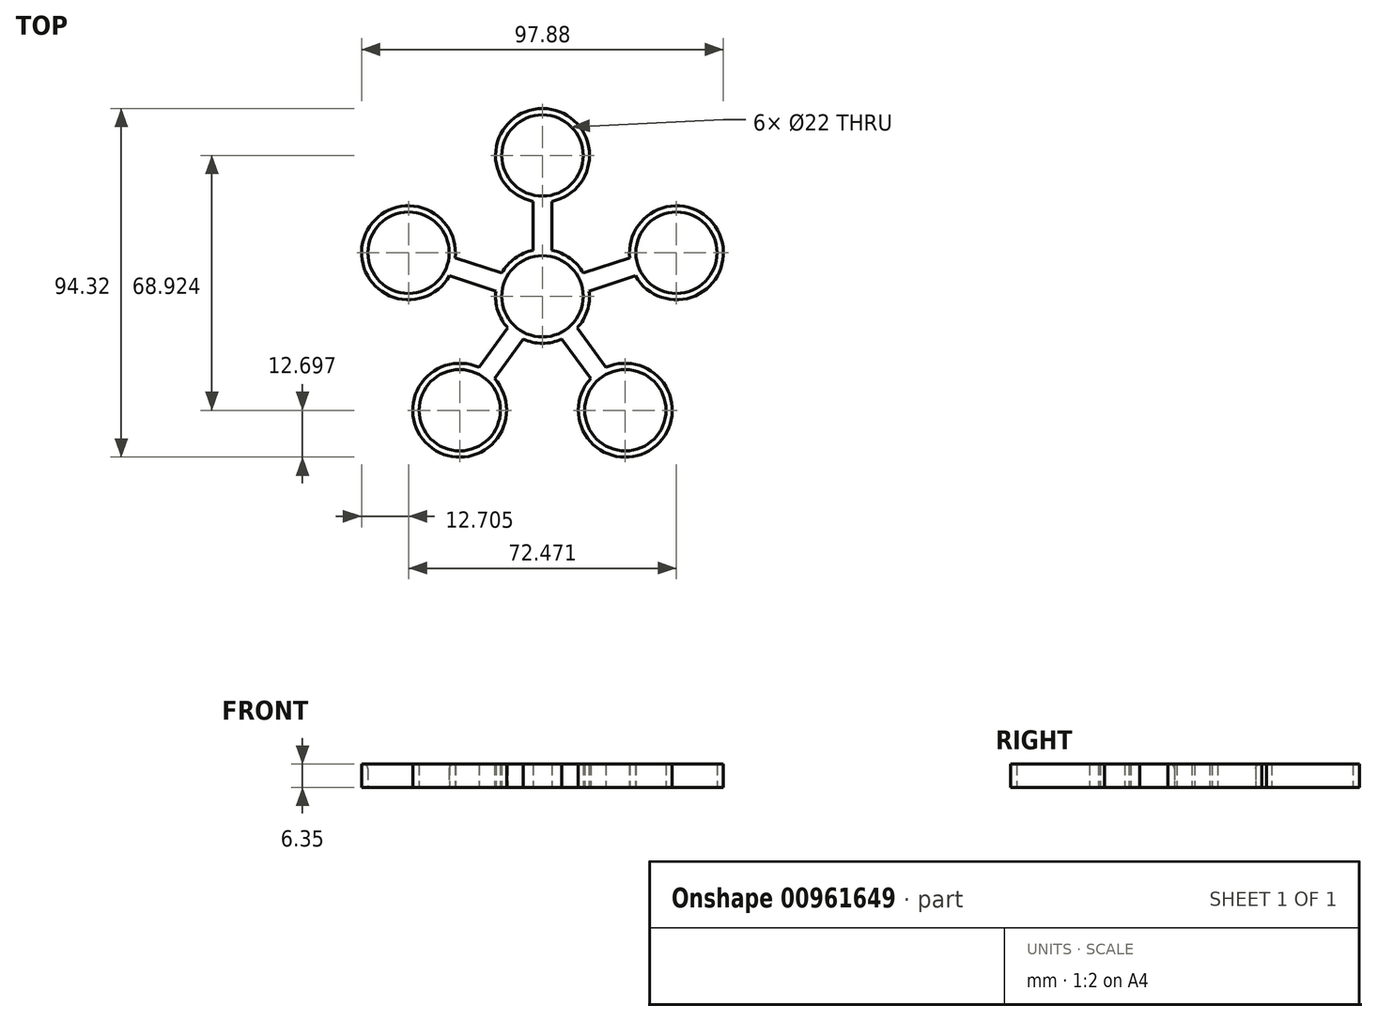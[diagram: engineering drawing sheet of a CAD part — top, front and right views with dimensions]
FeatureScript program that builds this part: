
annotation { "Feature Type Name" : "Feature", "Feature Type Description" : "" }
export const myFeature = defineFeature(function(context is Context, id is Id, definition is map)
    precondition{}
    {
        {
            var Q0;
            Q0=qCreatedBy(makeId("Top.planeOp"),FACE);
            var sketch = newSketch(context, id + "F0", { "sketchPlane" : qUnion([Q0])});
            skCircle(sketch, "E0", {"center": v(0, 0) * mm, "radius": 11 * mm});
            skArc(sketch, "E1", {"start": v(-2.54, 12.44) * mm, "mid": v(-7.46, 10.27) * mm, "end": v(-11.05, 6.26) * mm});
            skArc(sketch, "E2", {"start": v(2.54, 25.66) * mm, "mid": v(0, 50.8) * mm, "end": v(-2.54, 25.66) * mm});
            skCircle(sketch, "E3", {"center": v(0, 38.1) * mm, "radius": 11 * mm});
            skLineSegment(sketch, "E4", {"start": v(2.54, 25.66) * mm, "end": v(2.54, 12.44) * mm});
            skLineSegment(sketch, "E5", {"start": v(-2.54, 25.66) * mm, "end": v(-2.54, 12.44) * mm});
            skLineSegment(sketch, "E6.1.0", {"start": v(-23.62, 10.34) * mm, "end": v(-11.05, 6.26) * mm});
            skLineSegment(sketch, "E6.1.1", {"start": v(-25.19, 5.51) * mm, "end": v(-12.62, 1.43) * mm});
            skArc(sketch, "E6.1.2", {"start": v(-23.62, 10.34) * mm, "mid": v(-48.31, 15.7) * mm, "end": v(-25.19, 5.51) * mm});
            skCircle(sketch, "E6.1.3", {"center": v(-36.24, 11.77) * mm, "radius": 11 * mm});
            skLineSegment(sketch, "E6.2.0", {"start": v(-17.14, -19.26) * mm, "end": v(-9.37, -8.57) * mm});
            skLineSegment(sketch, "E6.2.1", {"start": v(-13.03, -22.25) * mm, "end": v(-5.26, -11.56) * mm});
            skArc(sketch, "E6.2.2", {"start": v(-17.14, -19.26) * mm, "mid": v(-29.86, -41.1) * mm, "end": v(-13.03, -22.25) * mm});
            skCircle(sketch, "E6.2.3", {"center": v(-22.4, -30.82) * mm, "radius": 11 * mm});
            skLineSegment(sketch, "E6.3.0", {"start": v(13.03, -22.25) * mm, "end": v(5.26, -11.56) * mm});
            skLineSegment(sketch, "E6.3.1", {"start": v(17.14, -19.26) * mm, "end": v(9.37, -8.57) * mm});
            skArc(sketch, "E6.3.2", {"start": v(13.03, -22.25) * mm, "mid": v(29.86, -41.1) * mm, "end": v(17.14, -19.26) * mm});
            skCircle(sketch, "E6.3.3", {"center": v(22.4, -30.82) * mm, "radius": 11 * mm});
            skLineSegment(sketch, "E6.4.0", {"start": v(25.19, 5.51) * mm, "end": v(12.62, 1.43) * mm});
            skLineSegment(sketch, "E6.4.1", {"start": v(23.62, 10.34) * mm, "end": v(11.05, 6.26) * mm});
            skArc(sketch, "E6.4.2", {"start": v(25.19, 5.51) * mm, "mid": v(48.31, 15.7) * mm, "end": v(23.62, 10.34) * mm});
            skCircle(sketch, "E6.4.3", {"center": v(36.24, 11.77) * mm, "radius": 11 * mm});
            skArc(sketch, "E7.trimOffspring", {"start": v(-12.62, 1.43) * mm, "mid": v(-12.08, -3.92) * mm, "end": v(-9.37, -8.57) * mm});
            skArc(sketch, "E8.trimOffspring", {"start": v(-5.26, -11.56) * mm, "mid": v(0, -12.7) * mm, "end": v(5.26, -11.56) * mm});
            skArc(sketch, "E9.trimOffspring", {"start": v(9.37, -8.57) * mm, "mid": v(12.08, -3.92) * mm, "end": v(12.62, 1.43) * mm});
            skArc(sketch, "E10.trimOffspring", {"start": v(11.05, 6.26) * mm, "mid": v(7.46, 10.27) * mm, "end": v(2.54, 12.44) * mm});
            skSolve(sketch);
        }
        {
            var Q0;
            Q0=makeQuery(id+"F0.imprint","IMPRINT",FACE,{"disambiguationData":[TD([[makeQuery(id+"F0.imprint","IMPRINT",EDGE,{"derivedFrom":sQuery(id+"F0.wireOp",EDGE,"E0")}),-1.0]])]});
            extrude(context, id + "F1", {"entities" : qUnion([Q0]), "depth" : 6.35 * mm, "offsetDistance" : 25.4 * mm});
        }
        {
            var Q0;
            Q0=makeQuery(id+"F1.opExtrude","CAP_EDGE",EDGE,{"disambiguationData":[OSD([sQuery(id+"F0.wireOp",EDGE,"E6.1.3")])],"isStart":false});
            fillet(context, id + "F2", {"entities" : qUnion([Q0]), "radius" : 1.27 * mm, "tangentPropagation" : true, "allowEdgeOverflow" : false});
        }
    });
